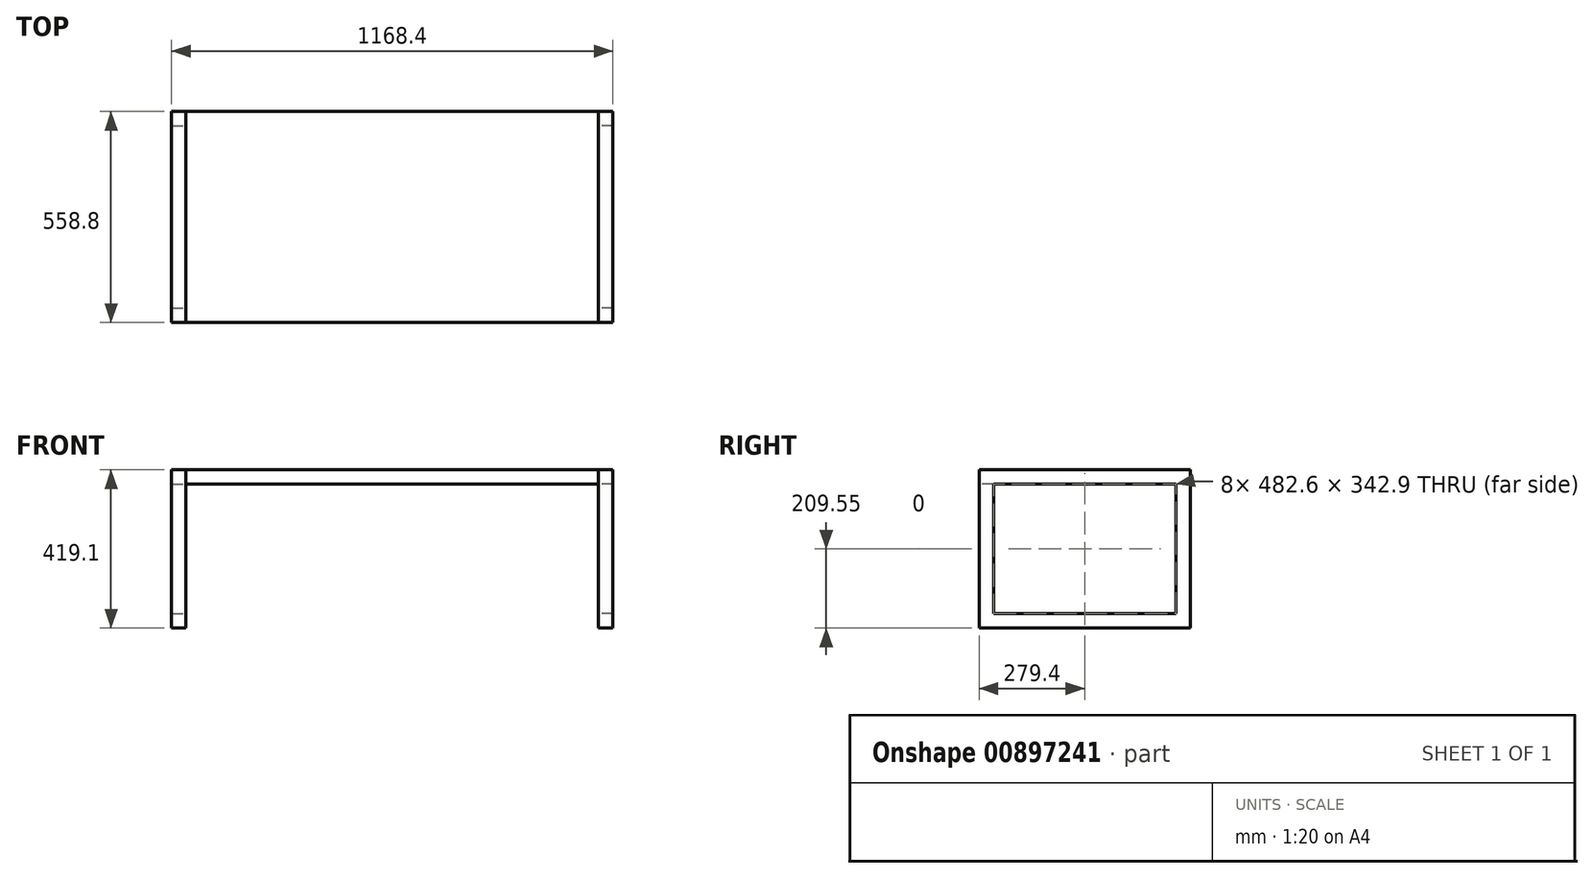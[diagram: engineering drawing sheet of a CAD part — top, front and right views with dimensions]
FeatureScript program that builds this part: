
annotation { "Feature Type Name" : "Feature", "Feature Type Description" : "" }
export const myFeature = defineFeature(function(context is Context, id is Id, definition is map)
    precondition{}
    {
        {
            var Q0;
            Q0=qCreatedBy(makeId("Top.planeOp"),FACE);
            var sketch = newSketch(context, id + "F0", { "sketchPlane" : qUnion([Q0])});
            skLineSegment(sketch, "E0.bottom", {"start": v(-546.1, 279.4) * mm, "end": v(546.1, 279.4) * mm});
            skLineSegment(sketch, "E0.top", {"start": v(-546.1, -279.4) * mm, "end": v(546.1, -279.4) * mm});
            skLineSegment(sketch, "E0.left", {"start": v(-546.1, 279.4) * mm, "end": v(-546.1, -279.4) * mm});
            skLineSegment(sketch, "E0.right", {"start": v(546.1, 279.4) * mm, "end": v(546.1, -279.4) * mm});
            skPoint(sketch, "E0.middle", {"position": v(0, 0) * mm});
            skSolve(sketch);
        }
        {
            var Q0;
            Q0=makeQuery(id+"F0.imprint","IMPRINT",FACE,{"disambiguationData":[TD([[makeQuery(id+"F0.imprint","IMPRINT",EDGE,{"derivedFrom":sQuery(id+"F0.wireOp",EDGE,"E0.bottom")}),-1.0]])]});
            extrude(context, id + "F1", {"entities" : qUnion([Q0]), "depth" : 38.1 * mm, "offsetDistance" : 25.4 * mm});
        }
        {
            var Q0;
            Q0=makeQuery(id+"F1.opExtrude","SWEPT_FACE",FACE,{"disambiguationData":[OSD([sQuery(id+"F0.wireOp",EDGE,"E0.left")])]});
            var sketch = newSketch(context, id + "F2", { "sketchPlane" : qUnion([Q0])});
            skLineSegment(sketch, "E1.bottom", {"start": v(-279.4, 38.1) * mm, "end": v(279.4, 38.1) * mm});
            skLineSegment(sketch, "E1.top", {"start": v(-279.4, -381) * mm, "end": v(279.4, -381) * mm});
            skLineSegment(sketch, "E1.left", {"start": v(-279.4, 38.1) * mm, "end": v(-279.4, -381) * mm});
            skLineSegment(sketch, "E1.right", {"start": v(279.4, 38.1) * mm, "end": v(279.4, -381) * mm});
            skLineSegment(sketch, "E2.0", {"start": v(-241.3, 0) * mm, "end": v(-241.3, -342.9) * mm});
            skLineSegment(sketch, "E2.1", {"start": v(-241.3, 0) * mm, "end": v(241.3, 0) * mm});
            skLineSegment(sketch, "E2.2", {"start": v(241.3, 0) * mm, "end": v(241.3, -342.9) * mm});
            skLineSegment(sketch, "E2.3", {"start": v(-241.3, -342.9) * mm, "end": v(241.3, -342.9) * mm});
            skSolve(sketch);
        }
        {
            var Q0;
            {var subQ4=sQuery(id+"F2.wireOp",EDGE,"E1.bottom");Q0=makeQuery(id+"F2.imprint","IMPRINT",FACE,{"disambiguationData":[TD([[makeQuery(id+"F2.imprint","IMPRINT",EDGE,{"derivedFrom":subQ4}),-1.0]])]});}
            var Q1;
            {var subQ3=sQuery(id+"F2.wireOp",EDGE,"E1.top");Q1=makeQuery(id+"F2.imprint","IMPRINT",FACE,{"disambiguationData":[TD([[makeQuery(id+"F2.imprint","IMPRINT",EDGE,{"derivedFrom":subQ3}),1.0]])]});}
            extrude(context, id + "F3", {"entities" : qUnion([Q0, Q1]), "depth" : 38.1 * mm, "offsetDistance" : 25.4 * mm});
        }
        {
            var Q0;
            Q0=makeQuery(id+"F3.opExtrude","SWEPT_BODY",BODY,{"disambiguationData":[OSD([sQuery(id+"F2.wireOp",EDGE,"E1.bottom"),sQuery(id+"F2.wireOp",EDGE,"E1.top"),sQuery(id+"F2.wireOp",EDGE,"E1.left"),sQuery(id+"F2.wireOp",EDGE,"E1.right"),sQuery(id+"F2.wireOp",EDGE,"E2.0"),sQuery(id+"F2.wireOp",EDGE,"E2.1"),sQuery(id+"F2.wireOp",EDGE,"E2.2"),sQuery(id+"F2.wireOp",EDGE,"E2.3")])]});
            var Q1;
            Q1=qCreatedBy(makeId("Right.planeOp"),FACE);
            mirror(context, id + "F4", {"entities" : qUnion([Q0]), "mirrorPlane" : qUnion([Q1])});
        }
    });
